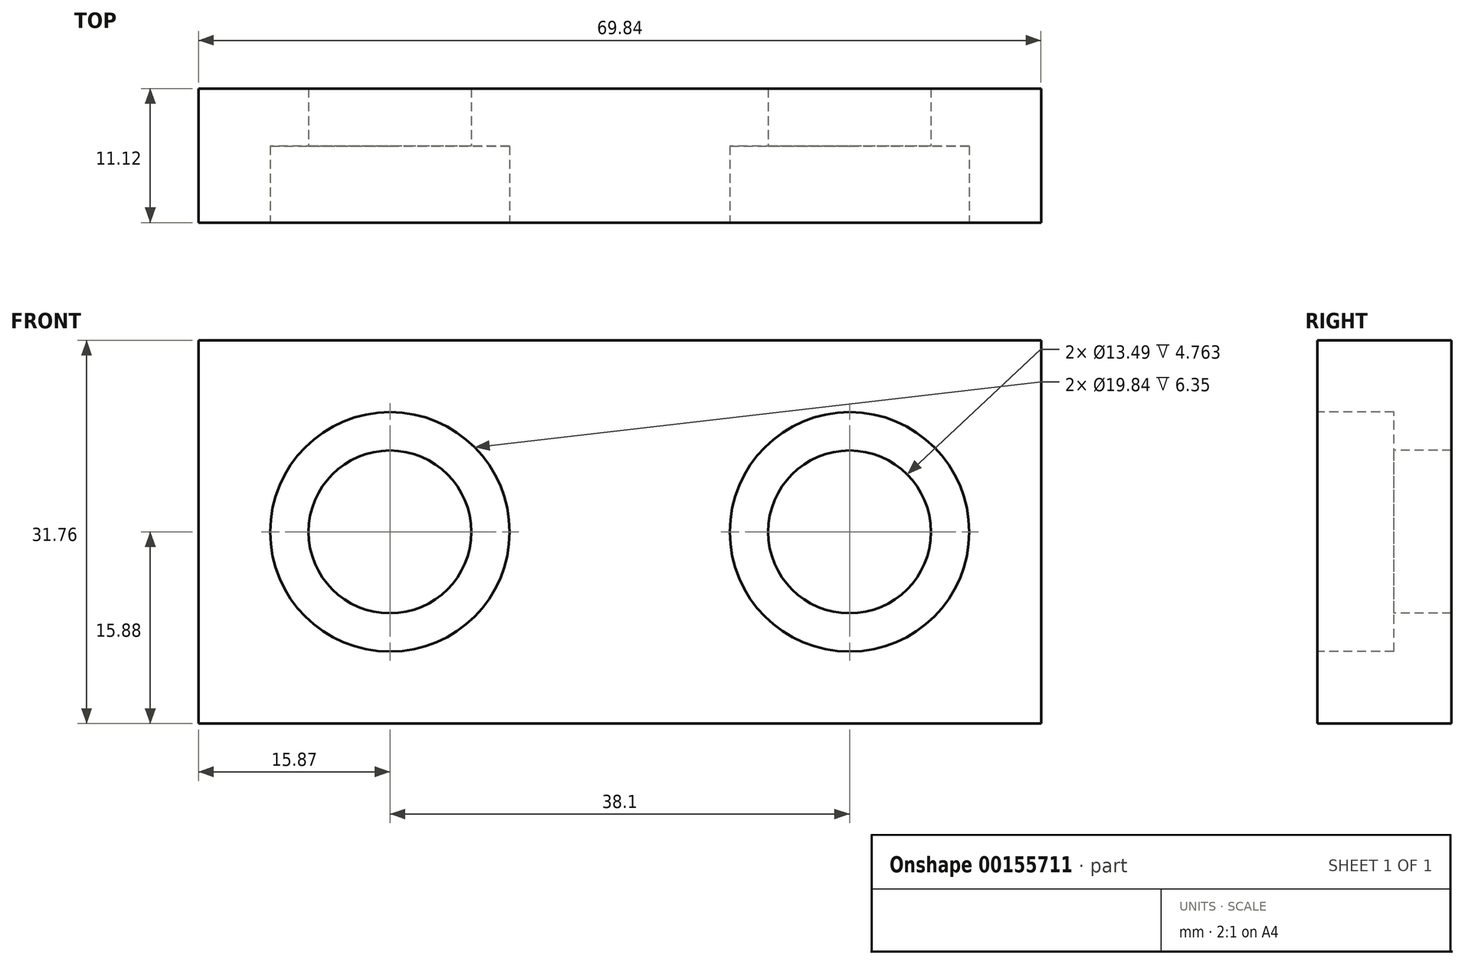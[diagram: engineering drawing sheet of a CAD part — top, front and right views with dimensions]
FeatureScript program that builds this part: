
annotation { "Feature Type Name" : "Feature", "Feature Type Description" : "" }
export const myFeature = defineFeature(function(context is Context, id is Id, definition is map)
    precondition{}
    {
        {
            var Q0;
            Q0=qCreatedBy(makeId("Front.planeOp"),FACE);
            var sketch = newSketch(context, id + "F0", { "sketchPlane" : qUnion([Q0])});
            skLineSegment(sketch, "E0.bottom", {"start": v(34.93, -15.87) * mm, "end": v(-34.93, -15.88) * mm});
            skLineSegment(sketch, "E0.top", {"start": v(34.93, 15.88) * mm, "end": v(-34.93, 15.88) * mm});
            skLineSegment(sketch, "E0.left", {"start": v(34.93, -15.87) * mm, "end": v(34.93, 15.88) * mm});
            skLineSegment(sketch, "E0.right", {"start": v(-34.93, -15.88) * mm, "end": v(-34.93, 15.88) * mm});
            skPoint(sketch, "E0.middle", {"position": v(0, 0) * mm});
            skSolve(sketch);
        }
        {
            var Q0;
            Q0 = qSketchRegion(id + "F0", true);
            extrude(context, id + "F1", {"entities" : qUnion([Q0]), "endBound" : BoundingType.SYMMETRIC, "depth" : 11.1 * mm});
        }
        {
            var Q0;
            Q0=makeQuery(id+"F1.opExtrude","CAP_FACE",FACE,{"disambiguationData":[OSD([sQuery(id+"F0.wireOp",EDGE,"E0.bottom"),sQuery(id+"F0.wireOp",EDGE,"E0.top"),sQuery(id+"F0.wireOp",EDGE,"E0.left"),sQuery(id+"F0.wireOp",EDGE,"E0.right")])],"isStart":false});
            var sketch = newSketch(context, id + "F2", { "sketchPlane" : qUnion([Q0])});
            skPoint(sketch, "E1", {"position": v(-19.05, 0) * mm});
            skPoint(sketch, "E2", {"position": v(19.05, 0) * mm});
            skSolve(sketch);
        }
        {
            var Q0;
            Q0=sQuery(id+"F2.wireOp",VERTEX,"E1");
            var Q1;
            Q1=sQuery(id+"F2.wireOp",VERTEX,"E2");
            var Q2;
            Q2=makeQuery(id+"F1.opExtrude","SWEPT_BODY",BODY,{"disambiguationData":[OSD([sQuery(id+"F0.wireOp",EDGE,"E0.bottom"),sQuery(id+"F0.wireOp",EDGE,"E0.top"),sQuery(id+"F0.wireOp",EDGE,"E0.left"),sQuery(id+"F0.wireOp",EDGE,"E0.right")])]});
            hole(context, id + "F3", {"style" : HoleStyle.C_BORE, "endStyle" : HoleEndStyle.THROUGH, "holeDiameter" : 13.5 * mm, "cBoreDiameter" : 19.84 * mm, "cBoreDepth" : 6.35 * mm, "startFromSketch" : true, "locations" : qUnion([Q0, Q1]), "scope" : qUnion([Q2]), "isTappedThrough" : true});
        }
    });
